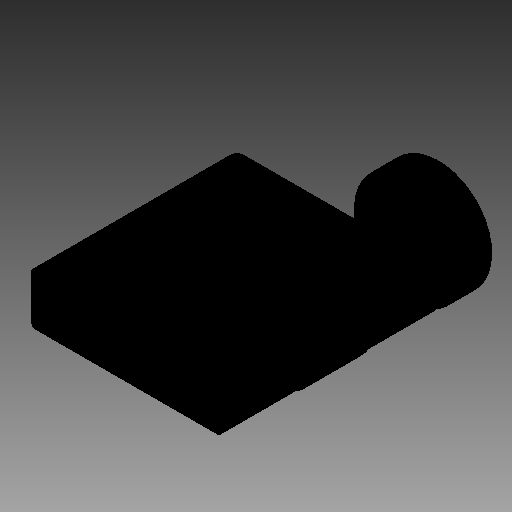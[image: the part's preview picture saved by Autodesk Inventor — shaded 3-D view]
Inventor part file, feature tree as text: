
AUTODESK INVENTOR PART (.ipt)
format: ipt  version: 2019 (Build 230136000, 136)  size: 221,696 bytes
history: native  units: in
note: dims shown in document units (in); Inventor stores cm internally (conversion verified against a paired STEP export)
features: other x35, sketch x9, extrude x7, revolve x2
ambient origin geometry x8: Origin, YZ Plane, XZ Plane, XY Plane, X Axis, Y Axis, Z Axis, Center Point
bodies: Solid1 (feature_tree)
feature tree (53):
  extrude  "Extrusion1"  Depth=1.5748in TaperAngle=0.0deg
  extrude  "Extrusion2"  Depth=1.5748in TaperAngle=0.0deg
  extrude  "Extrusion3"  TaperAngle=360.0deg  [1 undecoded]
  extrude  "Extrusion4"  TaperAngle=360.0deg  [1 undecoded]
  extrude  "Extrusion5"  [1 undecoded]
  revolve  "Revolution1"  [1 undecoded]
  extrude  "Extrusion6"  [1 undecoded]
  revolve  "Revolution2"  [1 undecoded]
  extrude  "Extrusion7"  [1 undecoded]
  other  "to_b_XY"
  other  "to_b_YZ"
  other  "to_b_ZX"
  other  "to_b_X"
  other  "to_b_Y"
  other  "to_b_Z"
  other  "to_b_Center"
  other  "to_pin_XY"
  other  "to_pin_YZ"
  other  "to_pin_ZX"
  other  "to_pin_X"
  other  "to_pin_Y"
  other  "to_pin_Z"
  other  "to_pin_Center"
  other  "to_washer1_XY"
  other  "to_washer1_YZ"
  other  "to_washer1_ZX"
  other  "to_washer1_X"
  other  "to_washer1_Y"
  other  "to_washer1_Z"
  other  "to_washer1_Center"
  other  "to_washer2_XY"
  other  "to_washer2_YZ"
  other  "to_washer2_ZX"
  other  "to_washer2_X"
  other  "to_washer2_Y"
  other  "to_washer2_Z"
  other  "to_washer2_Center"
  other  "to_washer3_XY"
  other  "to_washer3_YZ"
  other  "to_washer3_ZX"
  other  "to_washer3_X"
  other  "to_washer3_Y"
  other  "to_washer3_Z"
  other  "to_washer3_Center"
  sketch  "Sketch_1"  dims[d0=0.312in d1=0.0in d2=1.5748in d3=0.0in]
  sketch  "Sketch_2"  dims[d4=2.9134in d5=0.0in d6=1.5748in d7=0.0in]
  sketch  "Sketch_3"  dims[d8=0.462in d9=0.0in d10=360.0deg]
  sketch  "Sketch_4"  dims[d11=0.462in d12=0.0in d13=360.0deg]
  sketch  "Sketch_5"  dims[d14=1.5748in d15=0.0in]
  sketch  "Sketch_6"
  sketch  "Sketch_7"
  sketch  "Sketch_8"
  sketch  "Sketch_9"
note: 7 required parameter values undecoded (feature->parameter linkage not recoverable at this tier; creation-order binding heuristic only, values carry confidence <= 0.55)
